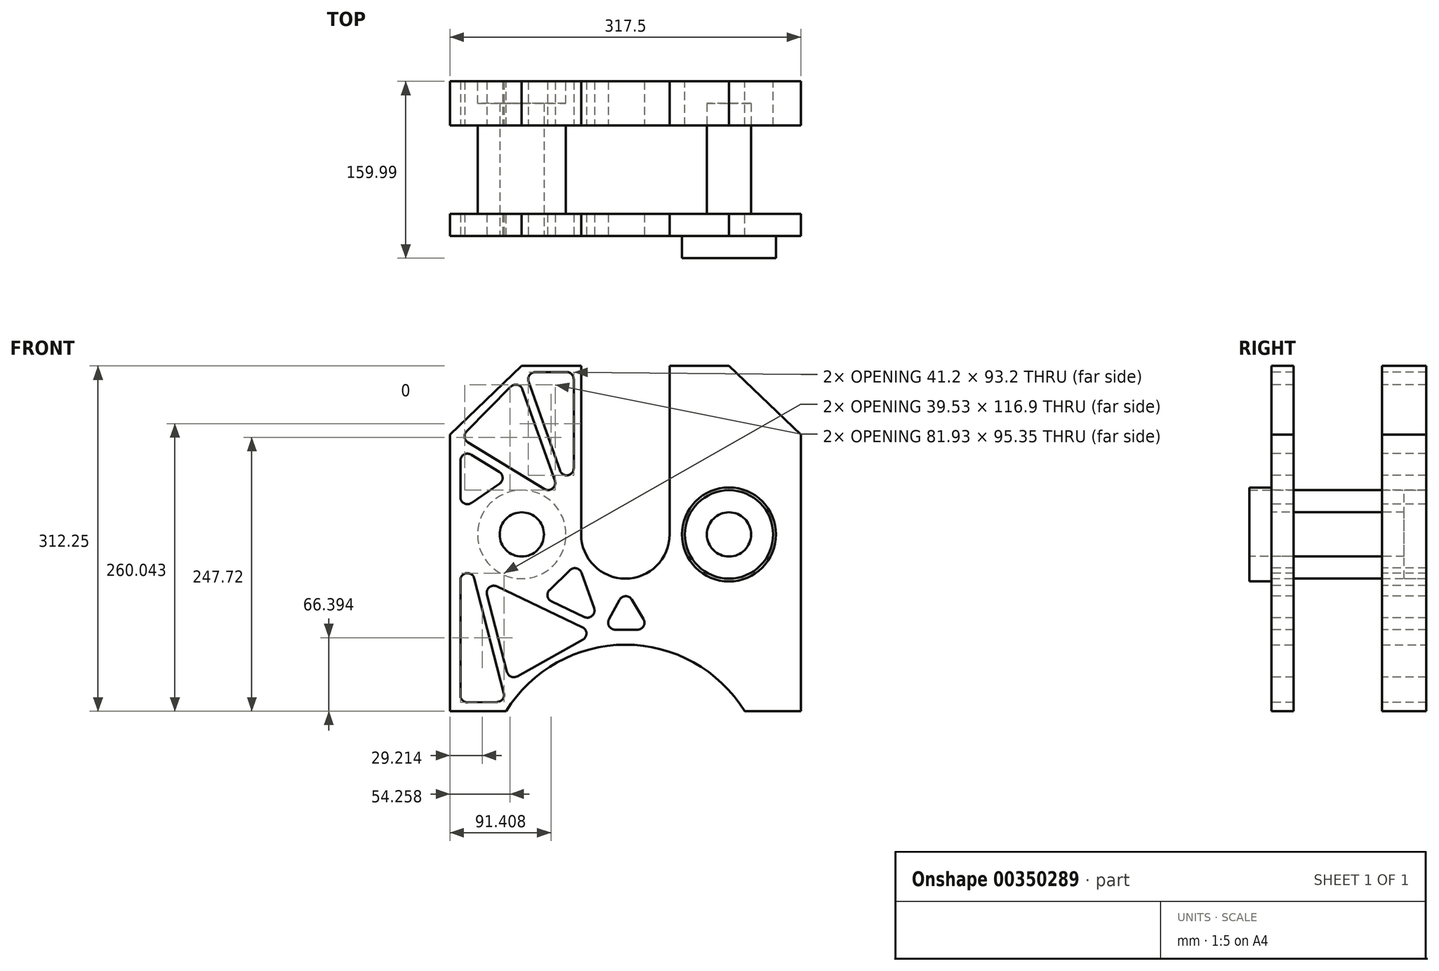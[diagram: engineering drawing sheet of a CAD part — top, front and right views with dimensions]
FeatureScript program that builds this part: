
annotation { "Feature Type Name" : "Feature", "Feature Type Description" : "" }
export const myFeature = defineFeature(function(context is Context, id is Id, definition is map)
    precondition{}
    {
        {
            var Q0;
            Q0=qCreatedBy(makeId("Front.planeOp"),FACE);
            var sketch = newSketch(context, id + "F0", { "sketchPlane" : qUnion([Q0])});
            skArc(sketch, "E0", {"start": v(107.95, 0) * mm, "mid": v(0, 60.1) * mm, "end": v(-107.95, 0) * mm});
            skLineSegment(sketch, "E1", {"start": v(107.95, 0) * mm, "end": v(158.75, 0) * mm});
            skLineSegment(sketch, "E2", {"start": v(158.75, 0) * mm, "end": v(158.75, 250.01) * mm});
            skLineSegment(sketch, "E3", {"start": v(158.75, 250.01) * mm, "end": v(93.75, 312.25) * mm});
            skLineSegment(sketch, "E4", {"start": v(93.75, 312.25) * mm, "end": v(40, 312.25) * mm});
            skLineSegment(sketch, "E5", {"start": v(40, 312.25) * mm, "end": v(40, 159.85) * mm});
            skCircle(sketch, "E6", {"center": v(93.75, 159.85) * mm, "radius": 40 * mm});
            skLineSegment(sketch, "E7.MirrorCS", {"start": v(-107.95, 0) * mm, "end": v(-158.75, 0) * mm});
            skCircle(sketch, "E8.MirrorC", {"center": v(-93.75, 159.85) * mm, "radius": 40 * mm});
            skLineSegment(sketch, "E9.MirrorCS", {"start": v(-158.75, 0) * mm, "end": v(-158.75, 250.01) * mm});
            skLineSegment(sketch, "E10.MirrorCS", {"start": v(-40, 312.25) * mm, "end": v(-40, 159.85) * mm});
            skLineSegment(sketch, "E11.MirrorCS", {"start": v(-158.75, 250.01) * mm, "end": v(-93.75, 312.25) * mm});
            skLineSegment(sketch, "E12.MirrorCS", {"start": v(-93.75, 312.25) * mm, "end": v(-40, 312.25) * mm});
            skArc(sketch, "E13", {"start": v(-40, 159.85) * mm, "mid": v(0, 119.85) * mm, "end": v(40, 159.85) * mm});
            skSolve(sketch);
        }
        {
            var Q0;
            Q0=makeQuery(id+"F0.imprint","IMPRINT",FACE,{"disambiguationData":[TD([[makeQuery(id+"F0.imprint","IMPRINT",EDGE,{"derivedFrom":sQuery(id+"F0.wireOp",EDGE,"E0")}),-1.0]])]});
            extrude(context, id + "F1", {"entities" : qUnion([Q0]), "depth" : 160 * mm});
        }
        {
            var Q0;
            Q0=makeQuery(id+"F1.opExtrude","SWEPT_FACE",FACE,{"disambiguationData":[OSD([sQuery(id+"F0.wireOp",EDGE,"E2")])]});
            var sketch = newSketch(context, id + "F2", { "sketchPlane" : qUnion([Q0])});
            skLineSegment(sketch, "E14.bottom", {"start": v(-120.02, 0) * mm, "end": v(-40, 0) * mm});
            skLineSegment(sketch, "E14.top", {"start": v(-120.02, 312.42) * mm, "end": v(-40, 312.42) * mm});
            skLineSegment(sketch, "E14.left", {"start": v(-120.02, 0) * mm, "end": v(-120.02, 312.42) * mm});
            skLineSegment(sketch, "E14.right", {"start": v(-40, 0) * mm, "end": v(-40, 312.42) * mm});
            skSolve(sketch);
        }
        {
            var Q0;
            {var subQ0=sQuery(id+"F2.wireOp",EDGE,"E14.top");Q0=makeQuery(id+"F2.imprint","IMPRINT",FACE,{"disambiguationData":[TD([[makeQuery(id+"F2.imprint","IMPRINT",EDGE,{"derivedFrom":subQ0}),-1.0]])]});}
            var Q1;
            {var subQ0=sQuery(id+"F2.wireOp",EDGE,"E14.bottom");Q1=makeQuery(id+"F2.imprint","IMPRINT",FACE,{"disambiguationData":[TD([[makeQuery(id+"F2.imprint","IMPRINT",EDGE,{"derivedFrom":subQ0}),1.0]])]});}
            extrude(context, id + "F3", {"entities" : qUnion([Q0, Q1]), "operationType" : NewBodyOperationType.REMOVE, "oppositeDirection" : true, "depth" : 398.78 * mm});
        }
        {
            var Q0;
            Q0=makeQuery(id+"F1.opExtrude","CAP_FACE",FACE,{"disambiguationData":[OSD([sQuery(id+"F0.wireOp",EDGE,"E0"),sQuery(id+"F0.wireOp",EDGE,"E1"),sQuery(id+"F0.wireOp",EDGE,"E2"),sQuery(id+"F0.wireOp",EDGE,"E3"),sQuery(id+"F0.wireOp",EDGE,"E4"),sQuery(id+"F0.wireOp",EDGE,"E5"),sQuery(id+"F0.wireOp",EDGE,"E6"),sQuery(id+"F0.wireOp",EDGE,"E7.MirrorCS"),sQuery(id+"F0.wireOp",EDGE,"E8.MirrorC"),sQuery(id+"F0.wireOp",EDGE,"E9.MirrorCS"),sQuery(id+"F0.wireOp",EDGE,"E10.MirrorCS"),sQuery(id+"F0.wireOp",EDGE,"E11.MirrorCS"),sQuery(id+"F0.wireOp",EDGE,"E12.MirrorCS"),sQuery(id+"F0.wireOp",EDGE,"E13")])],"isStart":false});
            var sketch = newSketch(context, id + "F4", { "sketchPlane" : qUnion([Q0])});
            skCircle(sketch, "E15", {"center": v(-93.75, 159.85) * mm, "radius": 20 * mm});
            skCircle(sketch, "E16", {"center": v(-93.75, 159.85) * mm, "radius": 42.5 * mm});
            skCircle(sketch, "E17.MirrorC", {"center": v(93.75, 159.85) * mm, "radius": 42.5 * mm});
            skCircle(sketch, "E18.MirrorC", {"center": v(93.75, 159.85) * mm, "radius": 20 * mm});
            skSolve(sketch);
        }
        {
            var Q0;
            Q0=makeQuery(id+"F4.imprint","IMPRINT",FACE,{"disambiguationData":[TD([[makeQuery(id+"F4.imprint","IMPRINT",EDGE,{"derivedFrom":sQuery(id+"F4.wireOp",EDGE,"E15")}),-1.0]])]});
            var Q1;
            Q1=makeQuery(id+"F4.imprint","IMPRINT",FACE,{"disambiguationData":[TD([[makeQuery(id+"F4.imprint","IMPRINT",EDGE,{"derivedFrom":sQuery(id+"F4.wireOp",EDGE,"E18.MirrorC")}),1.0]])]});
            extrude(context, id + "F5", {"entities" : qUnion([Q0, Q1]), "operationType" : NewBodyOperationType.ADD, "oppositeDirection" : true, "depth" : 140 * mm});
        }
        {
            var Q0;
            {var subQ0=sQuery(id+"F0.wireOp",EDGE,"E6");var subQ1=sQuery(id+"F0.wireOp",EDGE,"E8.MirrorC");Q0=makeQuery(id+"F5.boolean.opBoolean","MERGE",FACE,{"derivedFrom":[makeQuery(id+"F1.opExtrude","CAP_FACE",FACE,{"disambiguationData":[OSD([sQuery(id+"F0.wireOp",EDGE,"E0"),sQuery(id+"F0.wireOp",EDGE,"E1"),sQuery(id+"F0.wireOp",EDGE,"E2"),sQuery(id+"F0.wireOp",EDGE,"E3"),sQuery(id+"F0.wireOp",EDGE,"E4"),sQuery(id+"F0.wireOp",EDGE,"E5"),subQ0,sQuery(id+"F0.wireOp",EDGE,"E7.MirrorCS"),subQ1,sQuery(id+"F0.wireOp",EDGE,"E9.MirrorCS"),sQuery(id+"F0.wireOp",EDGE,"E10.MirrorCS"),sQuery(id+"F0.wireOp",EDGE,"E11.MirrorCS"),sQuery(id+"F0.wireOp",EDGE,"E12.MirrorCS"),sQuery(id+"F0.wireOp",EDGE,"E13")])],"isStart":false}),makeQuery(id+"F5.opExtrude","CAP_FACE",FACE,{"disambiguationData":[OSD([subQ1,sQuery(id+"F4.wireOp",EDGE,"E15")])],"isStart":true}),makeQuery(id+"F5.opExtrude","CAP_FACE",FACE,{"disambiguationData":[OSD([subQ0,sQuery(id+"F4.wireOp",EDGE,"E18.MirrorC")])],"isStart":true})]});}
            var sketch = newSketch(context, id + "F6", { "sketchPlane" : qUnion([Q0])});
            skCircle(sketch, "E19", {"center": v(-93.75, 159.85) * mm, "radius": 42.5 * mm});
            skCircle(sketch, "E20.MirrorC", {"center": v(93.75, 159.85) * mm, "radius": 42.5 * mm});
            skSolve(sketch);
        }
        {
            var Q0;
            Q0=makeQuery(id+"F6.imprint","IMPRINT",FACE,{"disambiguationData":[TD([[makeQuery(id+"F6.imprint","IMPRINT",EDGE,{"derivedFrom":sQuery(id+"F6.wireOp",EDGE,"E19")}),1.0]])]});
            var Q1;
            Q1=makeQuery(id+"F6.imprint","IMPRINT",FACE,{"disambiguationData":[TD([[makeQuery(id+"F6.imprint","IMPRINT",EDGE,{"derivedFrom":sQuery(id+"F6.wireOp",EDGE,"E20.MirrorC")}),-1.0]])]});
            extrude(context, id + "F7", {"entities" : qUnion([Q0, Q1]), "operationType" : NewBodyOperationType.REMOVE, "oppositeDirection" : true, "depth" : 19.99 * mm});
        }
        {
            var Q0;
            {var subQ0=sQuery(id+"F0.wireOp",EDGE,"E6");var subQ1=sQuery(id+"F0.wireOp",EDGE,"E8.MirrorC");Q0=makeQuery(id+"F5.boolean.opBoolean","MERGE",FACE,{"derivedFrom":[makeQuery(id+"F1.opExtrude","CAP_FACE",FACE,{"disambiguationData":[OSD([sQuery(id+"F0.wireOp",EDGE,"E0"),sQuery(id+"F0.wireOp",EDGE,"E1"),sQuery(id+"F0.wireOp",EDGE,"E2"),sQuery(id+"F0.wireOp",EDGE,"E3"),sQuery(id+"F0.wireOp",EDGE,"E4"),sQuery(id+"F0.wireOp",EDGE,"E5"),subQ0,sQuery(id+"F0.wireOp",EDGE,"E7.MirrorCS"),subQ1,sQuery(id+"F0.wireOp",EDGE,"E9.MirrorCS"),sQuery(id+"F0.wireOp",EDGE,"E10.MirrorCS"),sQuery(id+"F0.wireOp",EDGE,"E11.MirrorCS"),sQuery(id+"F0.wireOp",EDGE,"E12.MirrorCS"),sQuery(id+"F0.wireOp",EDGE,"E13")])],"isStart":false}),makeQuery(id+"F5.opExtrude","CAP_FACE",FACE,{"disambiguationData":[OSD([subQ1,sQuery(id+"F4.wireOp",EDGE,"E15")])],"isStart":true}),makeQuery(id+"F5.opExtrude","CAP_FACE",FACE,{"disambiguationData":[OSD([subQ0,sQuery(id+"F4.wireOp",EDGE,"E18.MirrorC")])],"isStart":true})]});}
            var sketch = newSketch(context, id + "F8", { "sketchPlane" : qUnion([Q0])});
            skLineSegment(sketch, "E21", {"start": v(-46.74, 219.7) * mm, "end": v(-46.74, 300.3) * mm});
            skLineSegment(sketch, "E22", {"start": v(-53.1, 306.64) * mm, "end": v(-81.63, 306.64) * mm});
            skLineSegment(sketch, "E23", {"start": v(-87.61, 298.17) * mm, "end": v(-59.08, 217.58) * mm});
            skLineSegment(sketch, "E24", {"start": v(-103.66, 293.51) * mm, "end": v(-143.66, 253.07) * mm});
            skLineSegment(sketch, "E25", {"start": v(-93.16, 291.17) * mm, "end": v(-63.89, 208.5) * mm});
            skLineSegment(sketch, "E26", {"start": v(-73.18, 200.96) * mm, "end": v(-142.45, 243.18) * mm});
            skLineSegment(sketch, "E27", {"start": v(-139.65, 231.99) * mm, "end": v(-114.12, 216.43) * mm});
            skLineSegment(sketch, "E28", {"start": v(-113.85, 205.76) * mm, "end": v(-139.37, 188.34) * mm});
            skLineSegment(sketch, "E29", {"start": v(-149.3, 193.58) * mm, "end": v(-149.3, 226.57) * mm});
            skLineSegment(sketch, "E30", {"start": v(-149.3, 14.3) * mm, "end": v(-149.3, 118.54) * mm});
            skPoint(sketch, "E30.startSnap0", {"position": v(-149.3, 209.71) * mm});
            skLineSegment(sketch, "E31", {"start": v(-136.8, 120.13) * mm, "end": v(-109.97, 16.27) * mm});
            skLineSegment(sketch, "E32", {"start": v(-116.03, 8.33) * mm, "end": v(-142.86, 7.94) * mm});
            skLineSegment(sketch, "E33", {"start": v(-125.22, 105.54) * mm, "end": v(-107.12, 35.46) * mm});
            skPoint(sketch, "E33.startSnap0", {"position": v(-128.63, 8.15) * mm});
            skLineSegment(sketch, "E34", {"start": v(-97.87, 31.5) * mm, "end": v(-38.5, 64.7) * mm});
            skLineSegment(sketch, "E35", {"start": v(-38.86, 75.97) * mm, "end": v(-116.35, 112.87) * mm});
            skLineSegment(sketch, "E36", {"start": v(-66.94, 99.37) * mm, "end": v(-37.06, 85.14) * mm});
            skLineSegment(sketch, "E37", {"start": v(-28.34, 93) * mm, "end": v(-39.73, 125.14) * mm});
            skLineSegment(sketch, "E38", {"start": v(-50.13, 127.58) * mm, "end": v(-68.63, 109.66) * mm});
            skPoint(sketch, "E39.visualSharp", {"position": v(-90.61, 306.64) * mm});
            skArc(sketch, "E39.filletArc", {"start": v(-81.63, 306.64) * mm, "mid": v(-86.81, 303.96) * mm, "end": v(-87.61, 298.17) * mm});
            skPoint(sketch, "E40.visualSharp", {"position": v(-46.74, 306.64) * mm});
            skArc(sketch, "E40.filletArc", {"start": v(-46.74, 300.3) * mm, "mid": v(-48.6, 304.78) * mm, "end": v(-53.1, 306.64) * mm});
            skPoint(sketch, "E41.visualSharp", {"position": v(-46.74, 182.74) * mm});
            skArc(sketch, "E41.filletArc", {"start": v(-59.08, 217.58) * mm, "mid": v(-52.01, 213.44) * mm, "end": v(-46.74, 219.7) * mm});
            skPoint(sketch, "E42.visualSharp", {"position": v(-57.93, 191.66) * mm});
            skArc(sketch, "E42.filletArc", {"start": v(-73.18, 200.96) * mm, "mid": v(-65.87, 201.45) * mm, "end": v(-63.89, 208.5) * mm});
            skPoint(sketch, "E43.visualSharp", {"position": v(-149.3, 247.36) * mm});
            skArc(sketch, "E43.filletArc", {"start": v(-143.66, 253.07) * mm, "mid": v(-145.44, 247.83) * mm, "end": v(-142.45, 243.18) * mm});
            skPoint(sketch, "E44.visualSharp", {"position": v(-149.3, 237.87) * mm});
            skArc(sketch, "E44.filletArc", {"start": v(-139.65, 231.99) * mm, "mid": v(-146.06, 232.1) * mm, "end": v(-149.3, 226.57) * mm});
            skPoint(sketch, "E45.visualSharp", {"position": v(-149.3, 181.55) * mm});
            skArc(sketch, "E45.filletArc", {"start": v(-149.3, 193.58) * mm, "mid": v(-145.92, 187.96) * mm, "end": v(-139.37, 188.34) * mm});
            skPoint(sketch, "E46.visualSharp", {"position": v(-105.72, 211.31) * mm});
            skArc(sketch, "E46.filletArc", {"start": v(-113.85, 205.76) * mm, "mid": v(-111.08, 211.17) * mm, "end": v(-114.12, 216.43) * mm});
            skPoint(sketch, "E47.visualSharp", {"position": v(-96.54, 300.72) * mm});
            skArc(sketch, "E47.filletArc", {"start": v(-93.16, 291.17) * mm, "mid": v(-97.76, 295.25) * mm, "end": v(-103.66, 293.51) * mm});
            skPoint(sketch, "E48.visualSharp", {"position": v(-149.3, 168.51) * mm});
            skArc(sketch, "E48.filletArc", {"start": v(-136.8, 120.13) * mm, "mid": v(-143.75, 124.84) * mm, "end": v(-149.3, 118.54) * mm});
            skPoint(sketch, "E49.visualSharp", {"position": v(-128.63, 118.71) * mm});
            skArc(sketch, "E49.filletArc", {"start": v(-116.35, 112.87) * mm, "mid": v(-123.12, 112.03) * mm, "end": v(-125.22, 105.54) * mm});
            skPoint(sketch, "E50.visualSharp", {"position": v(-75.2, 103.3) * mm});
            skArc(sketch, "E50.filletArc", {"start": v(-68.63, 109.66) * mm, "mid": v(-70.48, 104.07) * mm, "end": v(-66.94, 99.37) * mm});
            skPoint(sketch, "E51.visualSharp", {"position": v(-43.03, 134.47) * mm});
            skArc(sketch, "E51.filletArc", {"start": v(-39.73, 125.14) * mm, "mid": v(-44.26, 129.2) * mm, "end": v(-50.13, 127.58) * mm});
            skPoint(sketch, "E52.visualSharp", {"position": v(-23.23, 78.56) * mm});
            skArc(sketch, "E52.filletArc", {"start": v(-37.06, 85.14) * mm, "mid": v(-30.08, 86.16) * mm, "end": v(-28.34, 93) * mm});
            skPoint(sketch, "E53.visualSharp", {"position": v(-105.06, 27.5) * mm});
            skArc(sketch, "E53.filletArc", {"start": v(-107.12, 35.46) * mm, "mid": v(-103.47, 31.21) * mm, "end": v(-97.87, 31.5) * mm});
            skPoint(sketch, "E54.visualSharp", {"position": v(-27.77, 70.7) * mm});
            skArc(sketch, "E54.filletArc", {"start": v(-38.5, 64.7) * mm, "mid": v(-35.25, 70.45) * mm, "end": v(-38.86, 75.97) * mm});
            skPoint(sketch, "E55.visualSharp", {"position": v(-107.95, 8.44) * mm});
            skArc(sketch, "E55.filletArc", {"start": v(-116.03, 8.33) * mm, "mid": v(-111.07, 10.83) * mm, "end": v(-109.97, 16.27) * mm});
            skPoint(sketch, "E56.visualSharp", {"position": v(-149.3, 7.85) * mm});
            skArc(sketch, "E56.filletArc", {"start": v(-149.3, 14.3) * mm, "mid": v(-147.4, 9.77) * mm, "end": v(-142.86, 7.94) * mm});
            skArc(sketch, "E57.MirrorCS", {"start": v(149.3, 193.58) * mm, "mid": v(145.92, 187.96) * mm, "end": v(139.37, 188.34) * mm});
            skArc(sketch, "E58.MirrorCS", {"start": v(116.03, 8.33) * mm, "mid": v(111.07, 10.83) * mm, "end": v(109.97, 16.27) * mm});
            skArc(sketch, "E59.MirrorCS", {"start": v(81.63, 306.64) * mm, "mid": v(86.81, 303.96) * mm, "end": v(87.61, 298.17) * mm});
            skArc(sketch, "E60.MirrorCS", {"start": v(37.06, 85.14) * mm, "mid": v(30.08, 86.16) * mm, "end": v(28.34, 93) * mm});
            skArc(sketch, "E61.MirrorCS", {"start": v(39.73, 125.14) * mm, "mid": v(44.26, 129.2) * mm, "end": v(50.13, 127.58) * mm});
            skArc(sketch, "E62.MirrorCS", {"start": v(143.66, 253.07) * mm, "mid": v(145.44, 247.83) * mm, "end": v(142.45, 243.18) * mm});
            skArc(sketch, "E63.MirrorCS", {"start": v(116.35, 112.87) * mm, "mid": v(123.12, 112.03) * mm, "end": v(125.22, 105.54) * mm});
            skArc(sketch, "E64.MirrorCS", {"start": v(38.5, 64.7) * mm, "mid": v(35.25, 70.45) * mm, "end": v(38.86, 75.97) * mm});
            skArc(sketch, "E65.MirrorCS", {"start": v(113.85, 205.76) * mm, "mid": v(111.08, 211.17) * mm, "end": v(114.12, 216.43) * mm});
            skArc(sketch, "E66.MirrorCS", {"start": v(136.8, 120.13) * mm, "mid": v(143.75, 124.84) * mm, "end": v(149.3, 118.54) * mm});
            skArc(sketch, "E67.MirrorCS", {"start": v(139.65, 231.99) * mm, "mid": v(146.06, 232.1) * mm, "end": v(149.3, 226.57) * mm});
            skArc(sketch, "E68.MirrorCS", {"start": v(107.12, 35.46) * mm, "mid": v(103.47, 31.21) * mm, "end": v(97.87, 31.5) * mm});
            skArc(sketch, "E69.MirrorCS", {"start": v(68.63, 109.66) * mm, "mid": v(70.48, 104.07) * mm, "end": v(66.94, 99.37) * mm});
            skArc(sketch, "E70.MirrorCS", {"start": v(46.74, 300.3) * mm, "mid": v(48.6, 304.78) * mm, "end": v(53.1, 306.64) * mm});
            skArc(sketch, "E71.MirrorCS", {"start": v(149.3, 14.3) * mm, "mid": v(147.4, 9.77) * mm, "end": v(142.86, 7.94) * mm});
            skArc(sketch, "E72.MirrorCS", {"start": v(93.16, 291.17) * mm, "mid": v(97.76, 295.25) * mm, "end": v(103.66, 293.51) * mm});
            skArc(sketch, "E73.MirrorCS", {"start": v(73.18, 200.96) * mm, "mid": v(65.87, 201.45) * mm, "end": v(63.89, 208.5) * mm});
            skLineSegment(sketch, "E74.MirrorCS", {"start": v(149.3, 193.58) * mm, "end": v(149.3, 226.57) * mm});
            skLineSegment(sketch, "E75.MirrorCS", {"start": v(116.03, 8.33) * mm, "end": v(142.86, 7.94) * mm});
            skPoint(sketch, "E76.MirrorP", {"position": v(105.06, 27.5) * mm});
            skPoint(sketch, "E77.MirrorP", {"position": v(149.3, 181.55) * mm});
            skPoint(sketch, "E78.MirrorP", {"position": v(128.63, 8.15) * mm});
            skPoint(sketch, "E79.MirrorP", {"position": v(149.3, 247.36) * mm});
            skPoint(sketch, "E80.MirrorP", {"position": v(46.74, 306.64) * mm});
            skPoint(sketch, "E81.MirrorP", {"position": v(149.3, 7.85) * mm});
            skPoint(sketch, "E82.MirrorP", {"position": v(149.3, 168.51) * mm});
            skPoint(sketch, "E83.MirrorP", {"position": v(43.03, 134.47) * mm});
            skLineSegment(sketch, "E84.MirrorCS", {"start": v(97.87, 31.5) * mm, "end": v(38.5, 64.7) * mm});
            skLineSegment(sketch, "E85.MirrorCS", {"start": v(38.86, 75.97) * mm, "end": v(116.35, 112.87) * mm});
            skLineSegment(sketch, "E86.MirrorCS", {"start": v(46.74, 219.7) * mm, "end": v(46.74, 300.3) * mm});
            skLineSegment(sketch, "E87.MirrorCS", {"start": v(66.94, 99.37) * mm, "end": v(37.06, 85.14) * mm});
            skLineSegment(sketch, "E88.MirrorCS", {"start": v(53.1, 306.64) * mm, "end": v(81.63, 306.64) * mm});
            skPoint(sketch, "E89.MirrorP", {"position": v(149.3, 209.71) * mm});
            skPoint(sketch, "E90.MirrorP", {"position": v(105.72, 211.31) * mm});
            skPoint(sketch, "E91.MirrorP", {"position": v(27.77, 70.7) * mm});
            skLineSegment(sketch, "E92.MirrorCS", {"start": v(87.61, 298.17) * mm, "end": v(59.08, 217.58) * mm});
            skLineSegment(sketch, "E93.MirrorCS", {"start": v(103.66, 293.51) * mm, "end": v(143.66, 253.07) * mm});
            skLineSegment(sketch, "E94.MirrorCS", {"start": v(50.13, 127.58) * mm, "end": v(68.63, 109.66) * mm});
            skLineSegment(sketch, "E95.MirrorCS", {"start": v(93.16, 291.17) * mm, "end": v(63.89, 208.5) * mm});
            skLineSegment(sketch, "E96.MirrorCS", {"start": v(73.18, 200.96) * mm, "end": v(142.45, 243.18) * mm});
            skLineSegment(sketch, "E97.MirrorCS", {"start": v(139.65, 231.99) * mm, "end": v(114.12, 216.43) * mm});
            skPoint(sketch, "E98.MirrorP", {"position": v(23.23, 78.56) * mm});
            skPoint(sketch, "E99.MirrorP", {"position": v(128.63, 118.71) * mm});
            skPoint(sketch, "E100.MirrorP", {"position": v(57.93, 191.66) * mm});
            skLineSegment(sketch, "E101.MirrorCS", {"start": v(113.85, 205.76) * mm, "end": v(139.37, 188.34) * mm});
            skPoint(sketch, "E102.MirrorP", {"position": v(75.2, 103.3) * mm});
            skArc(sketch, "E103.MirrorCS", {"start": v(59.08, 217.58) * mm, "mid": v(52.01, 213.44) * mm, "end": v(46.74, 219.7) * mm});
            skLineSegment(sketch, "E104.MirrorCS", {"start": v(28.34, 93) * mm, "end": v(39.73, 125.14) * mm});
            skLineSegment(sketch, "E105.MirrorCS", {"start": v(149.3, 14.3) * mm, "end": v(149.3, 118.54) * mm});
            skPoint(sketch, "E106.MirrorP", {"position": v(107.95, 8.44) * mm});
            skPoint(sketch, "E107.MirrorP", {"position": v(46.74, 182.74) * mm});
            skPoint(sketch, "E108.MirrorP", {"position": v(149.3, 237.87) * mm});
            skPoint(sketch, "E109.MirrorP", {"position": v(96.54, 300.72) * mm});
            skPoint(sketch, "E110.MirrorP", {"position": v(90.61, 306.64) * mm});
            skLineSegment(sketch, "E111.MirrorCS", {"start": v(136.8, 120.13) * mm, "end": v(109.97, 16.27) * mm});
            skLineSegment(sketch, "E112.MirrorCS", {"start": v(125.22, 105.54) * mm, "end": v(107.12, 35.46) * mm});
            skLineSegment(sketch, "E113", {"start": v(-9.25, 73.7) * mm, "end": v(10.93, 73.7) * mm});
            skLineSegment(sketch, "E114", {"start": v(16.36, 83.33) * mm, "end": v(5.73, 100.95) * mm});
            skLineSegment(sketch, "E115", {"start": v(-5.29, 100.7) * mm, "end": v(-14.84, 83.07) * mm});
            skPoint(sketch, "E116.visualSharp", {"position": v(0, 110.45) * mm});
            skArc(sketch, "E116.filletArc", {"start": v(5.73, 100.95) * mm, "mid": v(0.15, 104.02) * mm, "end": v(-5.29, 100.7) * mm});
            skPoint(sketch, "E117.visualSharp", {"position": v(-19.92, 73.7) * mm});
            skArc(sketch, "E117.filletArc", {"start": v(-14.84, 83.07) * mm, "mid": v(-14.71, 76.8) * mm, "end": v(-9.25, 73.7) * mm});
            skPoint(sketch, "E118.visualSharp", {"position": v(22.17, 73.7) * mm});
            skArc(sketch, "E118.filletArc", {"start": v(10.93, 73.7) * mm, "mid": v(16.46, 76.92) * mm, "end": v(16.36, 83.33) * mm});
            skSolve(sketch);
        }
        {
            var Q0;
            Q0=makeQuery(id+"F8.imprint","IMPRINT",FACE,{"disambiguationData":[TD([[makeQuery(id+"F8.imprint","IMPRINT",EDGE,{"derivedFrom":sQuery(id+"F8.wireOp",EDGE,"E24")}),1.0]])]});
            var Q1;
            Q1=makeQuery(id+"F8.imprint","IMPRINT",FACE,{"disambiguationData":[TD([[makeQuery(id+"F8.imprint","IMPRINT",EDGE,{"derivedFrom":sQuery(id+"F8.wireOp",EDGE,"E21")}),1.0]])]});
            var Q2;
            Q2=makeQuery(id+"F8.imprint","IMPRINT",FACE,{"disambiguationData":[TD([[makeQuery(id+"F8.imprint","IMPRINT",EDGE,{"derivedFrom":sQuery(id+"F8.wireOp",EDGE,"E27")}),-1.0]])]});
            var Q3;
            Q3=makeQuery(id+"F8.imprint","IMPRINT",FACE,{"disambiguationData":[TD([[makeQuery(id+"F8.imprint","IMPRINT",EDGE,{"derivedFrom":sQuery(id+"F8.wireOp",EDGE,"E30")}),-1.0]])]});
            var Q4;
            Q4=makeQuery(id+"F8.imprint","IMPRINT",FACE,{"disambiguationData":[TD([[makeQuery(id+"F8.imprint","IMPRINT",EDGE,{"derivedFrom":sQuery(id+"F8.wireOp",EDGE,"E33")}),1.0]])]});
            var Q5;
            Q5=makeQuery(id+"F8.imprint","IMPRINT",FACE,{"disambiguationData":[TD([[makeQuery(id+"F8.imprint","IMPRINT",EDGE,{"derivedFrom":sQuery(id+"F8.wireOp",EDGE,"E36")}),1.0]])]});
            var Q6;
            Q6=makeQuery(id+"F8.imprint","IMPRINT",FACE,{"disambiguationData":[TD([[makeQuery(id+"F8.imprint","IMPRINT",EDGE,{"derivedFrom":sQuery(id+"F8.wireOp",EDGE,"E113")}),1.0]])]});
            var Q7;
            Q7=makeQuery(id+"F8.imprint","IMPRINT",FACE,{"disambiguationData":[TD([[makeQuery(id+"F8.imprint","IMPRINT",EDGE,{"derivedFrom":sQuery(id+"F8.wireOp",EDGE,"E60.MirrorCS")}),-1.0]])]});
            var Q8;
            Q8=makeQuery(id+"F8.imprint","IMPRINT",FACE,{"disambiguationData":[TD([[makeQuery(id+"F8.imprint","IMPRINT",EDGE,{"derivedFrom":sQuery(id+"F8.wireOp",EDGE,"E63.MirrorCS")}),-1.0]])]});
            var Q9;
            Q9=makeQuery(id+"F8.imprint","IMPRINT",FACE,{"disambiguationData":[TD([[makeQuery(id+"F8.imprint","IMPRINT",EDGE,{"derivedFrom":sQuery(id+"F8.wireOp",EDGE,"E58.MirrorCS")}),-1.0]])]});
            var Q10;
            Q10=makeQuery(id+"F8.imprint","IMPRINT",FACE,{"disambiguationData":[TD([[makeQuery(id+"F8.imprint","IMPRINT",EDGE,{"derivedFrom":sQuery(id+"F8.wireOp",EDGE,"E62.MirrorCS")}),-1.0]])]});
            var Q11;
            Q11=makeQuery(id+"F8.imprint","IMPRINT",FACE,{"disambiguationData":[TD([[makeQuery(id+"F8.imprint","IMPRINT",EDGE,{"derivedFrom":sQuery(id+"F8.wireOp",EDGE,"E59.MirrorCS")}),-1.0]])]});
            var Q12;
            Q12=makeQuery(id+"F8.imprint","IMPRINT",FACE,{"disambiguationData":[TD([[makeQuery(id+"F8.imprint","IMPRINT",EDGE,{"derivedFrom":sQuery(id+"F8.wireOp",EDGE,"E57.MirrorCS")}),-1.0]])]});
            extrude(context, id + "F9", {"entities" : qUnion([Q0, Q1, Q2, Q3, Q4, Q5, Q6, Q7, Q8, Q9, Q10, Q11, Q12]), "operationType" : NewBodyOperationType.REMOVE, "oppositeDirection" : true, "depth" : 294.13 * mm});
        }
    });
